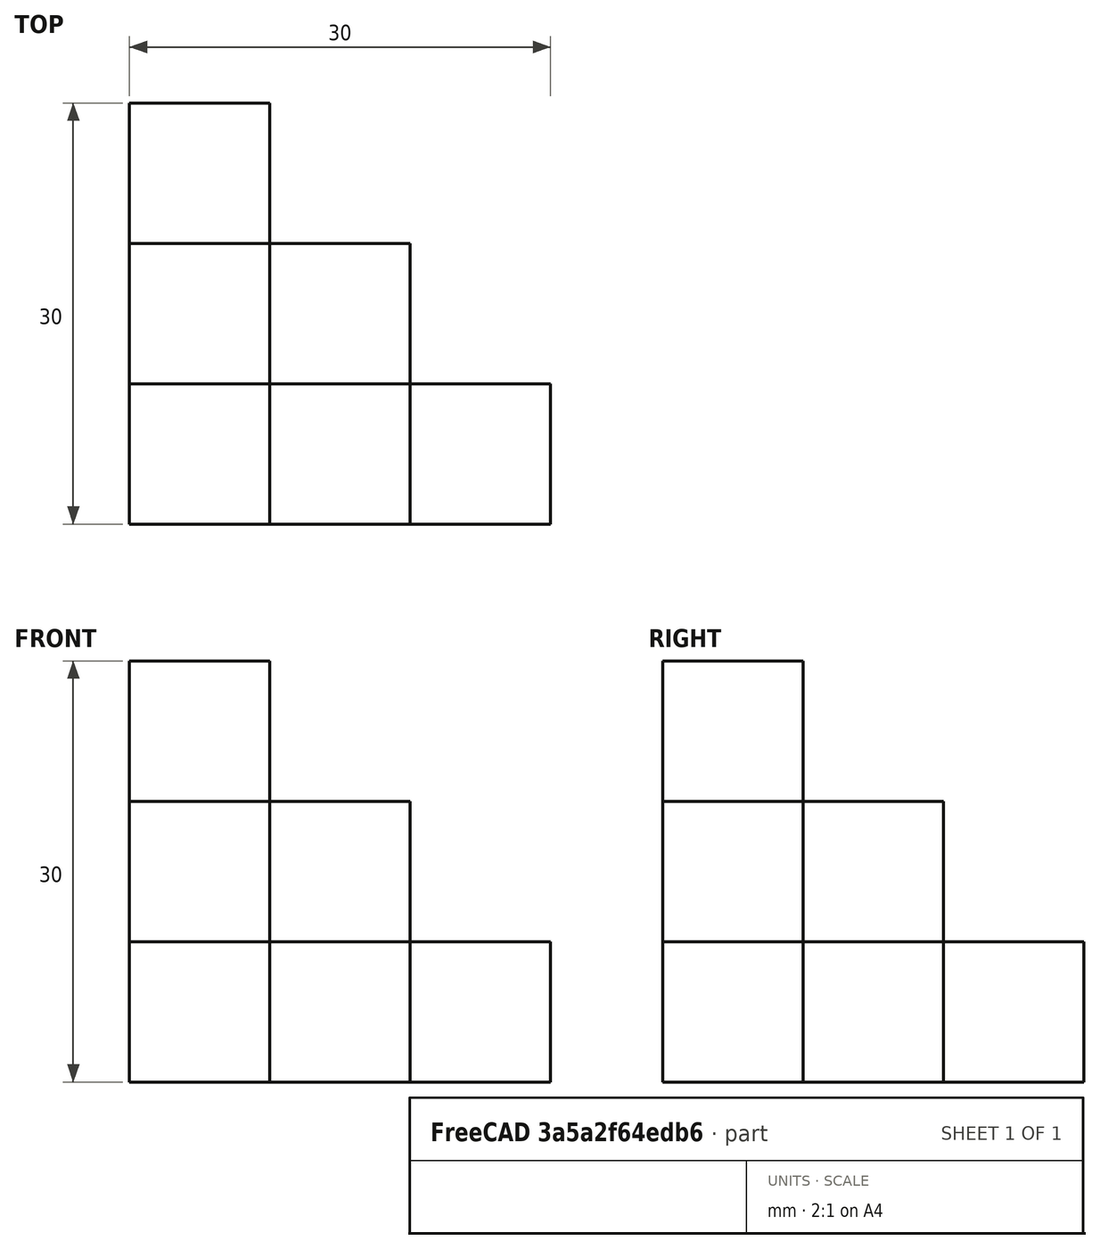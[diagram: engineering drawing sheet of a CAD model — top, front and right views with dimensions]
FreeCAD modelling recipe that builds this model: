
FCSTD DOCUMENT  (FreeCAD 0.20R29603 (Git))
Label: OJT1_T04R01_qubet
License: All rights reserved
LicenseURL: http://en.wikipedia.org/wiki/All_rights_reserved
objects: Part::Box×6
note: 6 computed .brp shape members not serialized (recipe doc carries the construction recipe); baked Part::Feature solids carry a one-line shape summary decoded from their .brp

FEATURE [Part::Box] Box  label="Cub"
  AttacherType = Attacher::AttachEngine3D
  Height = 10
  Length = 10
  Placement = pos=(0,0,10) rot=(0,0,1;0rad)
  Width = 10
FEATURE [Part::Box] Box001  label="Cub001"
  AttacherType = Attacher::AttachEngine3D
  Height = 10
  Length = 10
  Placement = pos=(10,0,0) rot=(0,0,1;0rad)
  Width = 10
FEATURE [Part::Box] Box002  label="Cub002"
  AttacherType = Attacher::AttachEngine3D
  Height = 10
  Length = 10
  Placement = pos=(0,10,0) rot=(0,0,1;0rad)
  Width = 10
FEATURE [Part::Box] Box003  label="Cub003"
  AttacherType = Attacher::AttachEngine3D
  Height = 10
  Length = 10
  Placement = pos=(20,0,-10) rot=(0,0,1;0rad)
  Width = 10
FEATURE [Part::Box] Box004  label="Cub004"
  AttacherType = Attacher::AttachEngine3D
  Height = 10
  Length = 10
  Placement = pos=(10,10,-10) rot=(0,0,1;0rad)
  Width = 10
FEATURE [Part::Box] Box005  label="Cub005"
  AttacherType = Attacher::AttachEngine3D
  Height = 10
  Length = 10
  Placement = pos=(0,20,-10) rot=(0,0,1;0rad)
  Width = 10
